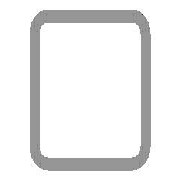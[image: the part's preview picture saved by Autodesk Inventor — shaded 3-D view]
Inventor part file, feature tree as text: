
AUTODESK INVENTOR PART (.ipt)
format: ipt  version: 2022.1 (Build 261234000, 234)  size: 134,144 bytes
history: native  units: mm (DEFAULTED — no unit token found)
features: other x4, sketch x3, extrude x1, plane x1
ambient origin geometry x8: Origin, YZ Plane, XZ Plane, XY Plane, X Axis, Y Axis, Z Axis, Center Point
bodies: Solid1 (feature_tree)
feature tree (9):
  parser-record x1  (decoder bookkeeping rows leaked as tree rows — omitted from the tree; the rows remain in map.json)
  other  "Driven Length"
  other  "Plano inicial"
  other  "Plano final"
  extrude  "Cuerpo"  TaperAngle=0.0deg  [1 undecoded]
  sketch  "Boceto"  dims[d10=40.0mm d11=40.0mm d12=5.0mm d13=-0.0mm d14=400.0mm d15=20.0mm d16=20.0mm d17=90.0deg d18=400.0mm]
  sketch  "Sketch3"  dims[d3=400.0mm d4=0.0mm]
  plane  "Work Plane3"
  sketch  "Sketch4"  dims[d7=7.5mm]
note: 1 required parameter value undecoded (feature->parameter linkage not recoverable at this tier; creation-order binding heuristic only, values carry confidence <= 0.55)
